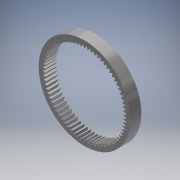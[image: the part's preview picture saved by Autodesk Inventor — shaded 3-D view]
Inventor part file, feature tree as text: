
AUTODESK INVENTOR PART (.ipt)
format: ipt  version: 2019 (Build 230136000, 136)  size: 463,360 bytes
history: native  units: mm (DEFAULTED — no unit token found)
features: plane x3, other x3, sketch x2, extrude x1
ambient origin geometry x8: Origin, YZ Plane, XZ Plane, XY Plane, X Axis, Y Axis, Z Axis, Center Point
bodies: Solid1 (feature_tree)
feature tree (9):
  extrude  "Extrusion1"  Depth=15.0mm TaperAngle=0.0deg
  plane  "Work Plane2"
  plane  "Work Plane8"
  plane  "Work Plane9"
  other  "正齒輪"
  sketch  "Sketch1"  dims[d0=123.430444mm d1=15.0mm d2=0.0mm]
  sketch  "Sketch2"  dims[d3=107.919785mm d4=10.0mm d5=0.0mm d16=37.698007mm d17=0.0mm d34=0.430355mm d39=0.0mm d45=0.0mm d47=37.698007mm d50=0.0mm d51=0.0mm d52=37.698007mm]
  other  "Srf1"
  other  "節圓直徑"
